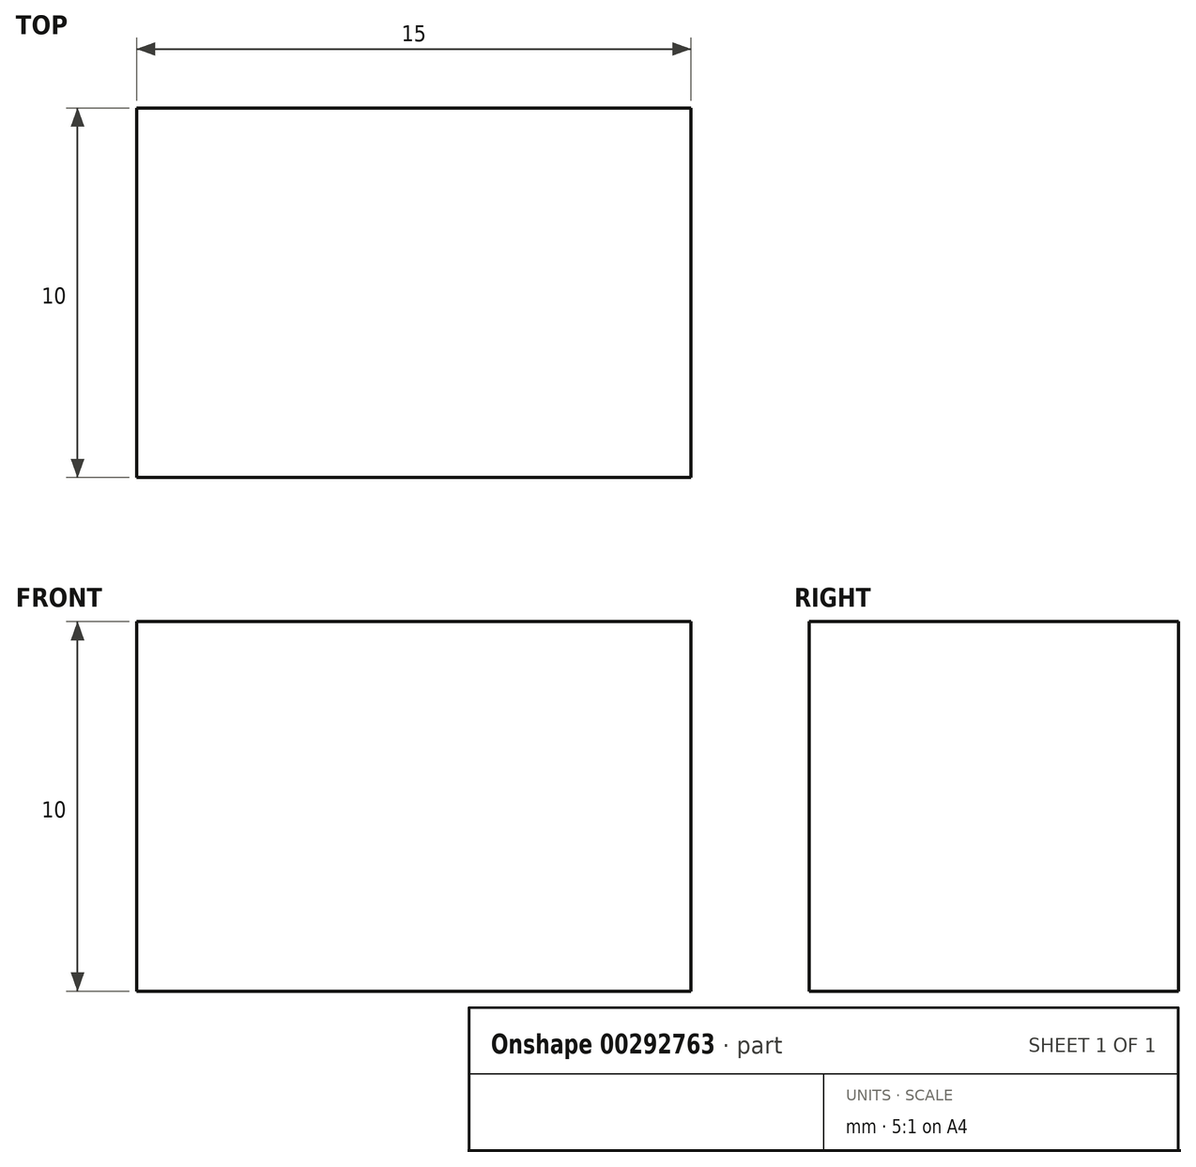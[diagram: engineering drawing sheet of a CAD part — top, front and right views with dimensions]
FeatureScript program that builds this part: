
annotation { "Feature Type Name" : "Feature", "Feature Type Description" : "" }
export const myFeature = defineFeature(function(context is Context, id is Id, definition is map)
    precondition{}
    {
        {
            var Q0;
            Q0=qCreatedBy(makeId("Front.planeOp"),FACE);
            var sketch = newSketch(context, id + "F0", { "sketchPlane" : qUnion([Q0])});
            skLineSegment(sketch, "E0", {"start": v(-64.82, 27.5) * mm, "end": v(-64.82, 17.5) * mm});
            skLineSegment(sketch, "E1", {"start": v(-64.82, 17.5) * mm, "end": v(-49.82, 17.5) * mm});
            skLineSegment(sketch, "E2", {"start": v(-64.82, 27.5) * mm, "end": v(-49.82, 27.5) * mm});
            skLineSegment(sketch, "E3", {"start": v(-49.82, 27.5) * mm, "end": v(-49.82, 17.5) * mm});
            skSolve(sketch);
        }
        {
            var Q0;
            Q0=makeQuery(id+"F0.imprint","IMPRINT",FACE,{"disambiguationData":[TD([[makeQuery(id+"F0.imprint","IMPRINT",EDGE,{"derivedFrom":sQuery(id+"F0.wireOp",EDGE,"E0")}),1.0]])]});
            extrude(context, id + "F1", {"entities" : qUnion([Q0]), "depth" : 10 * mm});
        }
    });
